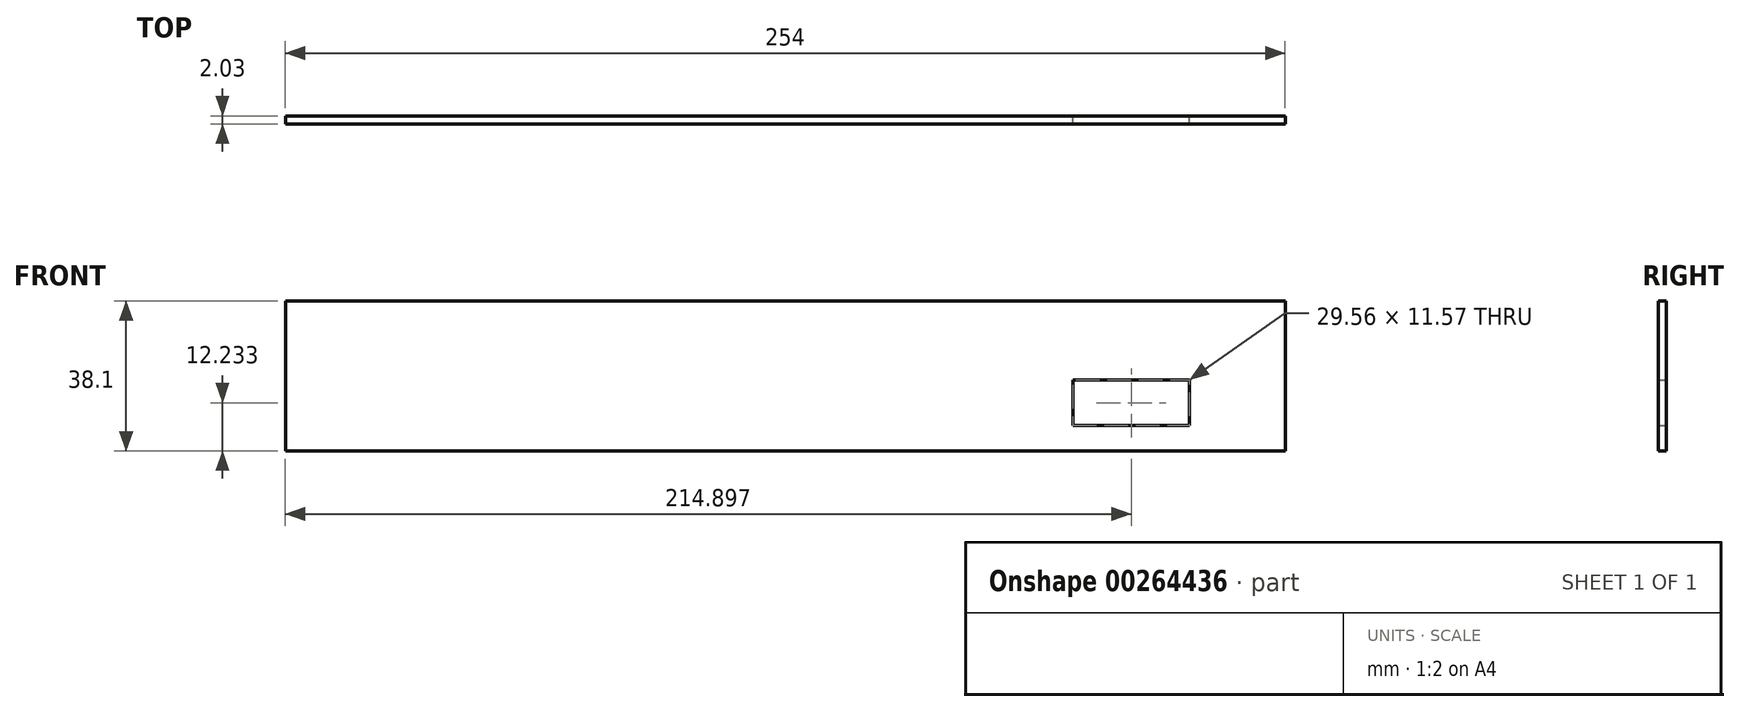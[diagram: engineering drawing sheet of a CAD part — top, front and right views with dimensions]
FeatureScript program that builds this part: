
annotation { "Feature Type Name" : "Feature", "Feature Type Description" : "" }
export const myFeature = defineFeature(function(context is Context, id is Id, definition is map)
    precondition{}
    {
        {
            var Q0;
            Q0=qCreatedBy(makeId("Front.planeOp"),FACE);
            var sketch = newSketch(context, id + "F0", { "sketchPlane" : qUnion([Q0])});
            skLineSegment(sketch, "E0.bottom", {"start": v(-123.33, 16.5) * mm, "end": v(146.28, 16.5) * mm});
            skLineSegment(sketch, "E0.top", {"start": v(-123.33, -21.6) * mm, "end": v(146.28, -21.6) * mm});
            skLineSegment(sketch, "E0.left", {"start": v(-123.33, 16.5) * mm, "end": v(-123.33, -21.6) * mm});
            skPoint(sketch, "E0.right.start.orphan", {"position": v(130.67, 16.5) * mm});
            skPoint(sketch, "E1.orphan", {"position": v(130.67, -21.6) * mm});
            skLineSegment(sketch, "E2", {"start": v(130.67, 16.5) * mm, "end": v(130.67, -21.6) * mm});
            skLineSegment(sketch, "E3", {"start": v(130.67, 16.5) * mm, "end": v(146.28, 16.5) * mm});
            skLineSegment(sketch, "E4", {"start": v(146.28, -21.6) * mm, "end": v(130.67, -21.6) * mm});
            skLineSegment(sketch, "E5.bottom", {"start": v(76.79, -3.57) * mm, "end": v(106.34, -3.57) * mm});
            skLineSegment(sketch, "E5.top", {"start": v(76.79, -15.14) * mm, "end": v(106.34, -15.14) * mm});
            skLineSegment(sketch, "E5.left", {"start": v(76.79, -3.57) * mm, "end": v(76.79, -15.14) * mm});
            skLineSegment(sketch, "E5.right", {"start": v(106.34, -3.57) * mm, "end": v(106.34, -15.14) * mm});
            skSolve(sketch);
        }
        {
            var Q0;
            Q0 = qSketchRegion(id + "F0", true);
            extrude(context, id + "F1", {"entities" : qUnion([Q0]), "depth" : 2.03 * mm});
        }
    });
